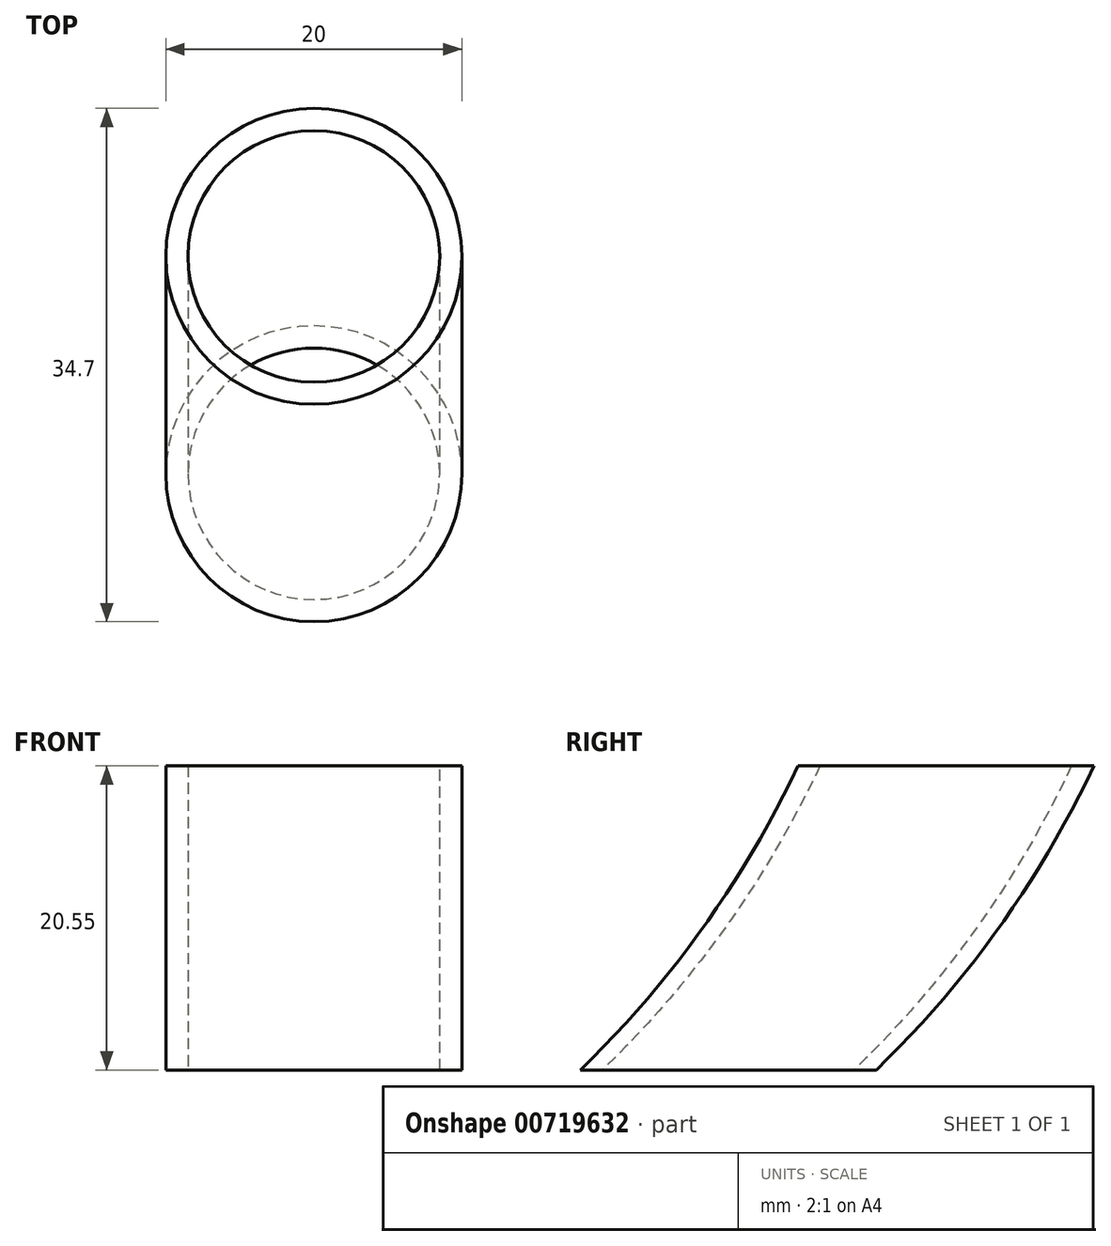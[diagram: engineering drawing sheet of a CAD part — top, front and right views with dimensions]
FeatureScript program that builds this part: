
annotation { "Feature Type Name" : "Feature", "Feature Type Description" : "" }
export const myFeature = defineFeature(function(context is Context, id is Id, definition is map)
    precondition{}
    {
        {
            var Q0;
            Q0=qCreatedBy(makeId("Top.planeOp"),FACE);
            var sketch = newSketch(context, id + "F0", { "sketchPlane" : qUnion([Q0])});
            skCircle(sketch, "E0", {"center": v(0, 0) * mm, "radius": 10 * mm});
            skCircle(sketch, "E1", {"center": v(0, 0) * mm, "radius": 8.5 * mm});
            skSolve(sketch);
        }
        {
            var Q0;
            Q0=qCreatedBy(makeId("Right.planeOp"),FACE);
            var sketch = newSketch(context, id + "F1", { "sketchPlane" : qUnion([Q0])});
            skArc(sketch, "E2", {"start": v(0, 0) * mm, "mid": v(8.29, 9.6) * mm, "end": v(14.7, 20.55) * mm});
            skSolve(sketch);
        }
        {
            var Q0;
            Q0 = qSketchRegion(id + "F0", true);
            var Q1;
            Q1 = qConstructionFilter(qBodyType(qCreatedBy(id + "F1" ,EDGE), BodyType.WIRE), ConstructionObject.NO);
            sweep(context, id + "F2", {"profiles" : qUnion([Q0]), "path" : qUnion([Q1]), "keepProfileOrientation" : true});
        }
    });
